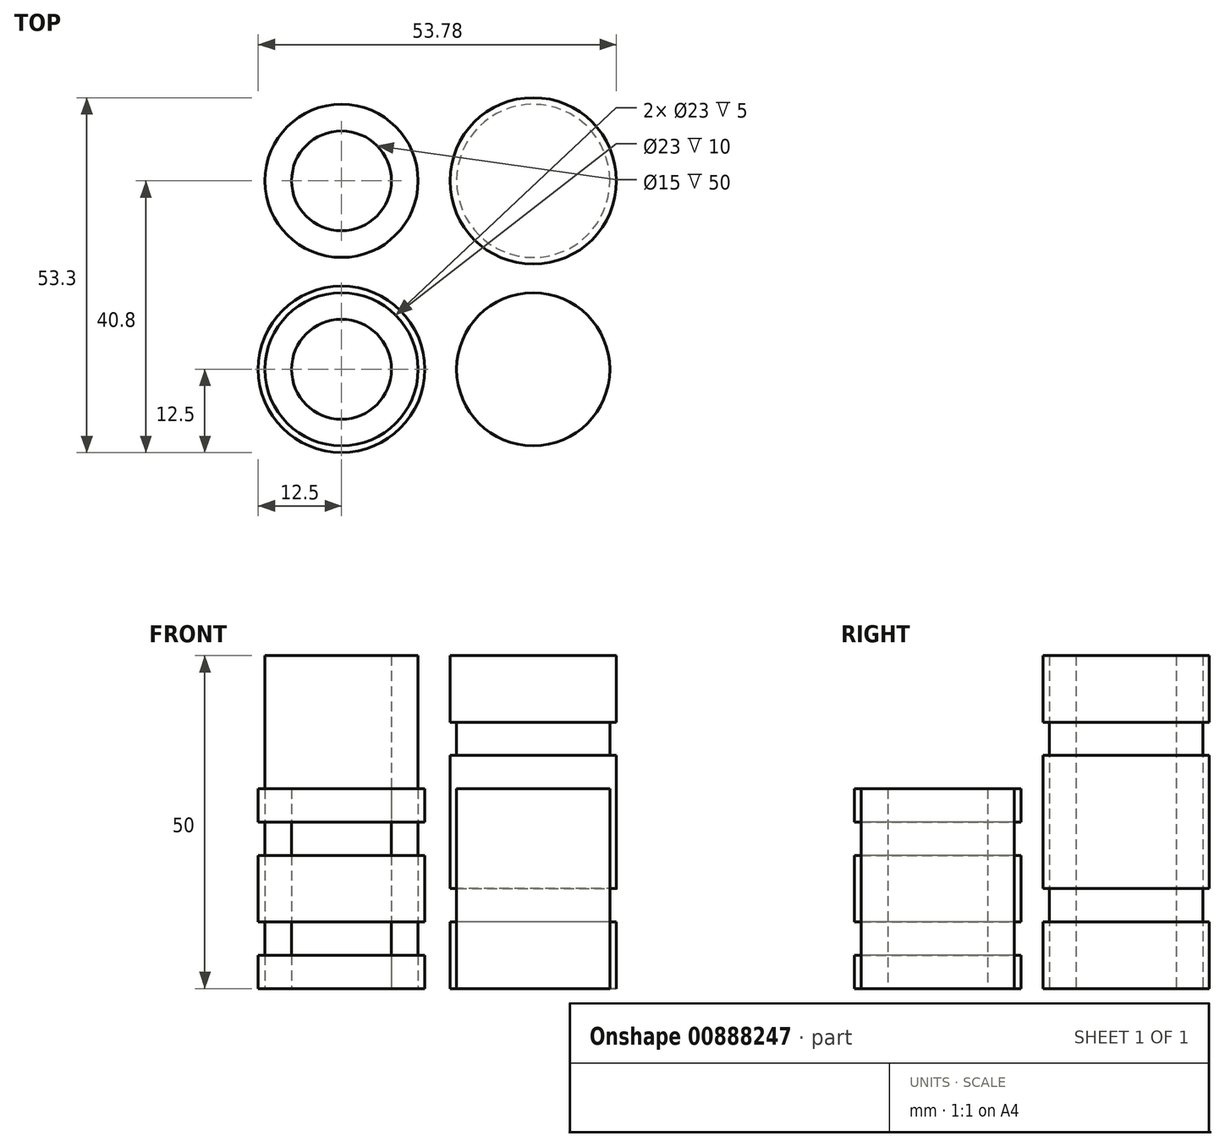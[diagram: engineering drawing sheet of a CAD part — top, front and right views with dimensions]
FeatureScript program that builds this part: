
annotation { "Feature Type Name" : "Feature", "Feature Type Description" : "" }
export const myFeature = defineFeature(function(context is Context, id is Id, definition is map)
    precondition{}
    {
        {
            var Q0;
            Q0=qCreatedBy(makeId("Top.planeOp"),FACE);
            var sketch = newSketch(context, id + "F0", { "sketchPlane" : qUnion([Q0])});
            skCircle(sketch, "E0", {"center": v(14.39, 14.15) * mm, "radius": 12.5 * mm});
            skCircle(sketch, "E1.MirrorC", {"center": v(-14.39, 14.15) * mm, "radius": 12.5 * mm});
            skCircle(sketch, "E2", {"center": v(-14.39, 14.15) * mm, "radius": 7.5 * mm});
            skCircle(sketch, "E3.MirrorC", {"center": v(-14.39, -14.15) * mm, "radius": 12.5 * mm});
            skCircle(sketch, "E4.MirrorC", {"center": v(14.39, -14.15) * mm, "radius": 12.5 * mm});
            skCircle(sketch, "E5.MirrorC", {"center": v(-14.39, -14.15) * mm, "radius": 7.5 * mm});
            skCircle(sketch, "E6", {"center": v(14.39, 14.15) * mm, "radius": 11.5 * mm});
            skCircle(sketch, "E7", {"center": v(-14.39, 14.15) * mm, "radius": 11.5 * mm});
            skCircle(sketch, "E8", {"center": v(-14.39, -14.15) * mm, "radius": 11.5 * mm});
            skCircle(sketch, "E9", {"center": v(14.39, -14.15) * mm, "radius": 11.5 * mm});
            skCircle(sketch, "E10", {"center": v(14.39, 14.15) * mm, "radius": 7.5 * mm});
            skCircle(sketch, "E11", {"center": v(14.39, -14.15) * mm, "radius": 7.5 * mm});
            skSolve(sketch);
        }
        {
            var Q0;
            Q0=makeQuery(id+"F0.imprint","IMPRINT",FACE,{"disambiguationData":[TD([[makeQuery(id+"F0.imprint","IMPRINT",EDGE,{"derivedFrom":sQuery(id+"F0.wireOp",EDGE,"E0")}),1.0]])]});
            var Q1;
            Q1=makeQuery(id+"F0.imprint","IMPRINT",FACE,{"disambiguationData":[TD([[makeQuery(id+"F0.imprint","IMPRINT",EDGE,{"derivedFrom":sQuery(id+"F0.wireOp",EDGE,"E1.MirrorC")}),-1.0]])]});
            var Q2;
            Q2=makeQuery(id+"F0.imprint","IMPRINT",FACE,{"disambiguationData":[TD([[makeQuery(id+"F0.imprint","IMPRINT",EDGE,{"derivedFrom":sQuery(id+"F0.wireOp",EDGE,"E2")}),-1.0]])]});
            var Q3;
            Q3=makeQuery(id+"F0.imprint","IMPRINT",FACE,{"disambiguationData":[TD([[makeQuery(id+"F0.imprint","IMPRINT",EDGE,{"derivedFrom":sQuery(id+"F0.wireOp",EDGE,"E6")}),1.0]])]});
            var Q4;
            Q4=makeQuery(id+"F0.imprint","IMPRINT",FACE,{"disambiguationData":[TD([[makeQuery(id+"F0.imprint","IMPRINT",EDGE,{"derivedFrom":sQuery(id+"F0.wireOp",EDGE,"E10")}),1.0]])]});
            extrude(context, id + "F1", {"entities" : qUnion([Q0, Q1, Q2, Q3, Q4]), "depth" : 50 * mm, "offsetDistance" : 25 * mm});
        }
        {
            var Q0;
            Q0=makeQuery(id+"F0.imprint","IMPRINT",FACE,{"disambiguationData":[TD([[makeQuery(id+"F0.imprint","IMPRINT",EDGE,{"derivedFrom":sQuery(id+"F0.wireOp",EDGE,"E4.MirrorC")}),-1.0]])]});
            var Q1;
            Q1=makeQuery(id+"F0.imprint","IMPRINT",FACE,{"disambiguationData":[TD([[makeQuery(id+"F0.imprint","IMPRINT",EDGE,{"derivedFrom":sQuery(id+"F0.wireOp",EDGE,"E3.MirrorC")}),1.0]])]});
            var Q2;
            Q2=makeQuery(id+"F0.imprint","IMPRINT",FACE,{"disambiguationData":[TD([[makeQuery(id+"F0.imprint","IMPRINT",EDGE,{"derivedFrom":sQuery(id+"F0.wireOp",EDGE,"E5.MirrorC")}),1.0]])]});
            var Q3;
            Q3=makeQuery(id+"F0.imprint","IMPRINT",FACE,{"disambiguationData":[TD([[makeQuery(id+"F0.imprint","IMPRINT",EDGE,{"derivedFrom":sQuery(id+"F0.wireOp",EDGE,"E9")}),1.0]])]});
            var Q4;
            Q4=makeQuery(id+"F0.imprint","IMPRINT",FACE,{"disambiguationData":[TD([[makeQuery(id+"F0.imprint","IMPRINT",EDGE,{"derivedFrom":sQuery(id+"F0.wireOp",EDGE,"E11")}),1.0]])]});
            extrude(context, id + "F2", {"entities" : qUnion([Q0, Q1, Q2, Q3, Q4]), "depth" : 30 * mm, "offsetDistance" : 25 * mm});
        }
        {
            var Q0;
            Q0=makeQuery(id+"F0.imprint","IMPRINT",FACE,{"disambiguationData":[TD([[makeQuery(id+"F0.imprint","IMPRINT",EDGE,{"derivedFrom":sQuery(id+"F0.wireOp",EDGE,"E1.MirrorC")}),-1.0]])]});
            var Q1;
            Q1=makeQuery(id+"F0.imprint","IMPRINT",FACE,{"disambiguationData":[TD([[makeQuery(id+"F0.imprint","IMPRINT",EDGE,{"derivedFrom":sQuery(id+"F0.wireOp",EDGE,"E0")}),1.0]])]});
            extrude(context, id + "F3", {"entities" : qUnion([Q0, Q1]), "operationType" : NewBodyOperationType.REMOVE, "depth" : 15 * mm, "offsetDistance" : 25 * mm, "hasSecondDirection" : true, "secondDirectionOppositeDirection" : false, "secondDirectionDepth" : 10 * mm});
        }
        {
            var Q0;
            Q0=makeQuery(id+"F0.imprint","IMPRINT",FACE,{"disambiguationData":[TD([[makeQuery(id+"F0.imprint","IMPRINT",EDGE,{"derivedFrom":sQuery(id+"F0.wireOp",EDGE,"E1.MirrorC")}),-1.0]])]});
            var Q1;
            Q1=makeQuery(id+"F0.imprint","IMPRINT",FACE,{"disambiguationData":[TD([[makeQuery(id+"F0.imprint","IMPRINT",EDGE,{"derivedFrom":sQuery(id+"F0.wireOp",EDGE,"E0")}),1.0]])]});
            extrude(context, id + "F4", {"entities" : qUnion([Q0, Q1]), "operationType" : NewBodyOperationType.REMOVE, "depth" : 40 * mm, "offsetDistance" : 25 * mm, "hasSecondDirection" : true, "secondDirectionOppositeDirection" : false, "secondDirectionDepth" : 35 * mm});
        }
        {
            var Q0;
            Q0=makeQuery(id+"F0.imprint","IMPRINT",FACE,{"disambiguationData":[TD([[makeQuery(id+"F0.imprint","IMPRINT",EDGE,{"derivedFrom":sQuery(id+"F0.wireOp",EDGE,"E3.MirrorC")}),1.0]])]});
            var Q1;
            Q1=makeQuery(id+"F0.imprint","IMPRINT",FACE,{"disambiguationData":[TD([[makeQuery(id+"F0.imprint","IMPRINT",EDGE,{"derivedFrom":sQuery(id+"F0.wireOp",EDGE,"E4.MirrorC")}),-1.0]])]});
            extrude(context, id + "F5", {"entities" : qUnion([Q0, Q1]), "operationType" : NewBodyOperationType.REMOVE, "depth" : 10 * mm, "offsetDistance" : 25 * mm, "hasSecondDirection" : true, "secondDirectionOppositeDirection" : false, "secondDirectionDepth" : 5 * mm});
        }
        {
            var Q0;
            Q0=makeQuery(id+"F0.imprint","IMPRINT",FACE,{"disambiguationData":[TD([[makeQuery(id+"F0.imprint","IMPRINT",EDGE,{"derivedFrom":sQuery(id+"F0.wireOp",EDGE,"E3.MirrorC")}),1.0]])]});
            var Q1;
            Q1=makeQuery(id+"F0.imprint","IMPRINT",FACE,{"disambiguationData":[TD([[makeQuery(id+"F0.imprint","IMPRINT",EDGE,{"derivedFrom":sQuery(id+"F0.wireOp",EDGE,"E4.MirrorC")}),-1.0]])]});
            extrude(context, id + "F6", {"entities" : qUnion([Q0, Q1]), "operationType" : NewBodyOperationType.REMOVE, "depth" : 25 * mm, "offsetDistance" : 25 * mm, "hasSecondDirection" : true, "secondDirectionOppositeDirection" : false, "secondDirectionDepth" : 20 * mm});
        }
    });
